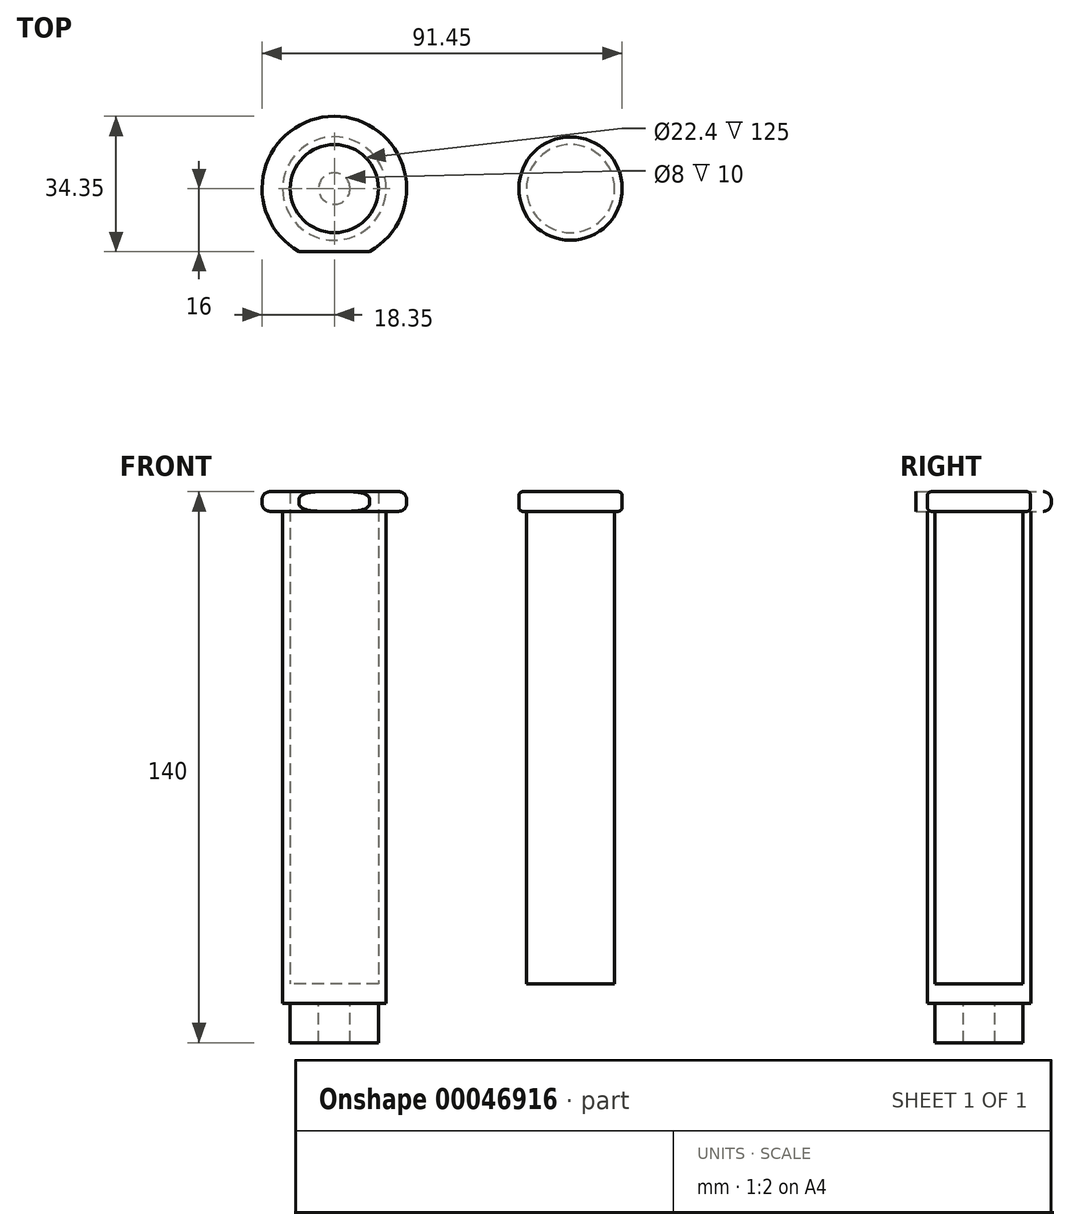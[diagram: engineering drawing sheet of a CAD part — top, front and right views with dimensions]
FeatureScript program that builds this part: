
annotation { "Feature Type Name" : "Feature", "Feature Type Description" : "" }
export const myFeature = defineFeature(function(context is Context, id is Id, definition is map)
    precondition{}
    {
        {
            var Q0;
            Q0=qCreatedBy(makeId("Top.planeOp"),FACE);
            var sketch = newSketch(context, id + "F0", { "sketchPlane" : qUnion([Q0])});
            skCircle(sketch, "E0", {"center": v(0, 0) * mm, "radius": 11.2 * mm});
            skCircle(sketch, "E1", {"center": v(0, 0) * mm, "radius": 18.35 * mm});
            skCircle(sketch, "E2", {"center": v(0, 0) * mm, "radius": 4 * mm});
            skCircle(sketch, "E3", {"center": v(0, 0) * mm, "radius": 13.15 * mm});
            skLineSegment(sketch, "E4", {"start": v(-8.98, -16) * mm, "end": v(8.98, -16) * mm});
            skSolve(sketch);
        }
        {
            var Q0;
            Q0=makeQuery(id+"F0.imprint","IMPRINT",FACE,{"disambiguationData":[TD([[makeQuery(id+"F0.imprint","IMPRINT",EDGE,{"derivedFrom":sQuery(id+"F0.wireOp",EDGE,"E0")}),-1.0]])]});
            var Q1;
            Q1=makeQuery(id+"F0.imprint","IMPRINT",FACE,{"disambiguationData":[TD([[makeQuery(id+"F0.imprint","IMPRINT",EDGE,{"derivedFrom":sQuery(id+"F0.wireOp",EDGE,"E3")}),-1.0]])]});
            extrude(context, id + "F1", {"entities" : qUnion([Q0, Q1]), "depth" : 5 * mm});
        }
        {
            var Q0;
            Q0=makeQuery(id+"F0.imprint","IMPRINT",FACE,{"disambiguationData":[TD([[makeQuery(id+"F0.imprint","IMPRINT",EDGE,{"derivedFrom":sQuery(id+"F0.wireOp",EDGE,"E0")}),-1.0]])]});
            extrude(context, id + "F2", {"entities" : qUnion([Q0]), "operationType" : NewBodyOperationType.ADD, "oppositeDirection" : true, "depth" : 120 * mm});
        }
        {
            var Q0;
            Q0=makeQuery(id+"F2.opExtrude","CAP_FACE",FACE,{"disambiguationData":[OSD([sQuery(id+"F0.wireOp",EDGE,"E0"),sQuery(id+"F0.wireOp",EDGE,"E3")])],"isStart":false});
            var sketch = newSketch(context, id + "F3", { "sketchPlane" : qUnion([Q0])});
            skCircle(sketch, "E5.0", {"center": v(0, 0) * mm, "radius": 13.15 * mm});
            skCircle(sketch, "E6.0", {"center": v(0, 0) * mm, "radius": 4 * mm});
            skSolve(sketch);
        }
        {
            var Q0;
            Q0=makeQuery(id+"F3.imprint","IMPRINT",FACE,{"disambiguationData":[TD([[makeQuery(id+"F3.imprint","IMPRINT",EDGE,{"derivedFrom":sQuery(id+"F3.wireOp",EDGE,"E5.0")}),-1.0]])]});
            var Q1;
            Q1=makeQuery(id+"F3.imprint","IMPRINT",FACE,{"disambiguationData":[TD([[makeQuery(id+"F3.imprint","IMPRINT",EDGE,{"derivedFrom":sQuery(id+"F3.wireOp",EDGE,"E6.0")}),1.0]])]});
            extrude(context, id + "F4", {"entities" : qUnion([Q0, Q1]), "operationType" : NewBodyOperationType.ADD, "depth" : 5 * mm});
        }
        {
            var Q0;
            Q0=makeQuery(id+"F3.imprint","IMPRINT",FACE,{"disambiguationData":[TD([[makeQuery(id+"F3.imprint","IMPRINT",EDGE,{"derivedFrom":sQuery(id+"F3.wireOp",EDGE,"E6.0")}),-1.0]])]});
            extrude(context, id + "F5", {"entities" : qUnion([Q0]), "operationType" : NewBodyOperationType.ADD, "depth" : 15 * mm});
        }
        {
            var Q0;
            Q0=makeQuery(id+"F1.opExtrude","CAP_EDGE",EDGE,{"disambiguationData":[OSD([sQuery(id+"F0.wireOp",EDGE,"E1")])],"isStart":false});
            var Q1;
            Q1=makeQuery(id+"F1.opExtrude","CAP_EDGE",EDGE,{"disambiguationData":[OSD([sQuery(id+"F0.wireOp",EDGE,"E1")])],"isStart":true});
            var Q2;
            Q2=makeQuery(id+"F2.opExtrude","CAP_EDGE",EDGE,{"disambiguationData":[OSD([sQuery(id+"F0.wireOp",EDGE,"E3")])],"isStart":true});
            fillet(context, id + "F6", {"entities" : qUnion([Q0, Q1, Q2]), "radius" : 2 * mm, "tangentPropagation" : true, "allowEdgeOverflow" : false});
        }
        {
            var Q0;
            Q0=qCreatedBy(makeId("Top.planeOp"),FACE);
            var sketch = newSketch(context, id + "F7", { "sketchPlane" : qUnion([Q0])});
            skCircle(sketch, "E7", {"center": v(60, 0) * mm, "radius": 11.2 * mm});
            skCircle(sketch, "E8", {"center": v(60, 0) * mm, "radius": 13.1 * mm});
            skSolve(sketch);
        }
        {
            var Q0;
            Q0=makeQuery(id+"F7.imprint","IMPRINT",FACE,{"disambiguationData":[TD([[makeQuery(id+"F7.imprint","IMPRINT",EDGE,{"derivedFrom":sQuery(id+"F7.wireOp",EDGE,"E7")}),-1.0]])]});
            var Q1;
            Q1=makeQuery(id+"F7.imprint","IMPRINT",FACE,{"disambiguationData":[TD([[makeQuery(id+"F7.imprint","IMPRINT",EDGE,{"derivedFrom":sQuery(id+"F7.wireOp",EDGE,"E7")}),1.0]])]});
            extrude(context, id + "F8", {"entities" : qUnion([Q0, Q1]), "depth" : 5 * mm});
        }
        {
            var Q0;
            Q0=makeQuery(id+"F7.imprint","IMPRINT",FACE,{"disambiguationData":[TD([[makeQuery(id+"F7.imprint","IMPRINT",EDGE,{"derivedFrom":sQuery(id+"F7.wireOp",EDGE,"E7")}),1.0]])]});
            extrude(context, id + "F9", {"entities" : qUnion([Q0]), "operationType" : NewBodyOperationType.ADD, "oppositeDirection" : true, "depth" : 120 * mm});
        }
        {
            var Q0;
            Q0=makeQuery(id+"F8.opExtrude","CAP_EDGE",EDGE,{"disambiguationData":[OSD([sQuery(id+"F7.wireOp",EDGE,"E8")])],"isStart":false});
            var Q1;
            Q1=makeQuery(id+"F8.opExtrude","CAP_EDGE",EDGE,{"disambiguationData":[OSD([sQuery(id+"F7.wireOp",EDGE,"E8")])],"isStart":true});
            fillet(context, id + "F10", {"entities" : qUnion([Q0, Q1]), "radius" : 1 * mm, "tangentPropagation" : true, "allowEdgeOverflow" : false});
        }
    });
